# Revit family: FU_Chair_Sandler_VARYA Task_2
name_source: partatom
category: Furniture
units: mm (PartAtom-declared; Revit-internal decimal feet)

## family parameters
Always vertical = No
Cut with Voids When Loaded = No
OmniClass Number = 23.21.23.15.17
Room Calculation Point = No
Shared = No
Work Plane-Based = Yes

## types (8) — shared parameters
401D = No
401G = No
BIMobject category = Chair
BIMobject category code = furniture-chair
BIMobject main category = Furniture
BIMobject main category code = furniture
Brand url = https://www.sandlerseating.com
Default Elevation = 1219.2 mm  [stored 4 ft]
Description = Chair
Design country = Brasil
Edition number = 1
Frame = BS23
Height Frame = 504 mm  [stored 1.65354 ft]
IFC Classification = Furnishing Element
Manufacturer = Sandler
Manufacturer country = USA
Manufacturer name = Sandler
Masterformat 2014 Code = 12 48 43.13
Masterformat 2014 Description = Chair Mats
OmniClass Code = 23-21 23 15 17
Product Guid = ??
Product SKU = ??
Product data url = https://www.sandlerseating.com
Product family = Furniture
Product group = Chair
QR code = https://www.sandlerseating.com
Uniformat II Description = Movable Furnishings

## per-type parameters (varying)
| type | Frame Material | Model | Product name | Seat Material | Shell | Shell Material | width |
| VARYA TASK 2.8 | M1_W01 - White | VARYA 3.2 | VARYA 3.2 | <By Category> | TP01 | Fabric - Aspect - Patagonia | 455 mm |
| VARYA TASK 2.7 | M1_B00 - Black | VARYA TASK 2.7 | VARYA TASK 2.7 | <By Category> | TP01 | Fabric - Aspect - Molokai | 560 mm |
| VARYA TASK 2.6 | Metal - Chrome - Polished | VARYA TASK 2.6 | VARYA TASK 2.6 | <By Category> | TP01 | Fabric - Aspect - Capones | 560 mm |
| VARYA TASK 2.5 | M1_W01 - White | VARYA TASK 2.5 | VARYA TASK 2.5 | <By Category> | TP01 | Fabric - Aspect - Amalfi | 560 mm |
| VARYA TASK 2.4 | M1_B00 - Black | VARYA TASK 2.4 | VARYA TASK 2.4 | Fabric - Aspect - Molokai | TP02 | Wood - Beech - Natural - V | 560 mm |
| VARYA TASK 2.3 | Metal - Chrome - Polished | VARYA TASK 2.3 | VARYA TASK 2.3 | <By Category> | TP01 | Wood - Beech - Wenge - V | 560 mm |
| VARYA TASK 2.2 | M1_W01 - White | VARYA TASK 2.2 | VARYA TASK 2.2 | Fabric - Aspect - Patagonia | TP02 | M2_V16 | 560 mm |
| VARYA TASK 2.1 | M1_B00 - Black | VARYA TASK 2.1 | VARYA TASK 2.1 | <By Category> | TP01 | M2_G42 | 560 mm |

note: [stored X ft] marks values corroborated as IEEE doubles in the binary element streams (Revit-internal decimal feet)

## geometry (parser evidence)
native form markers: Sweep x29
no freeform markers — native parametric forms only
